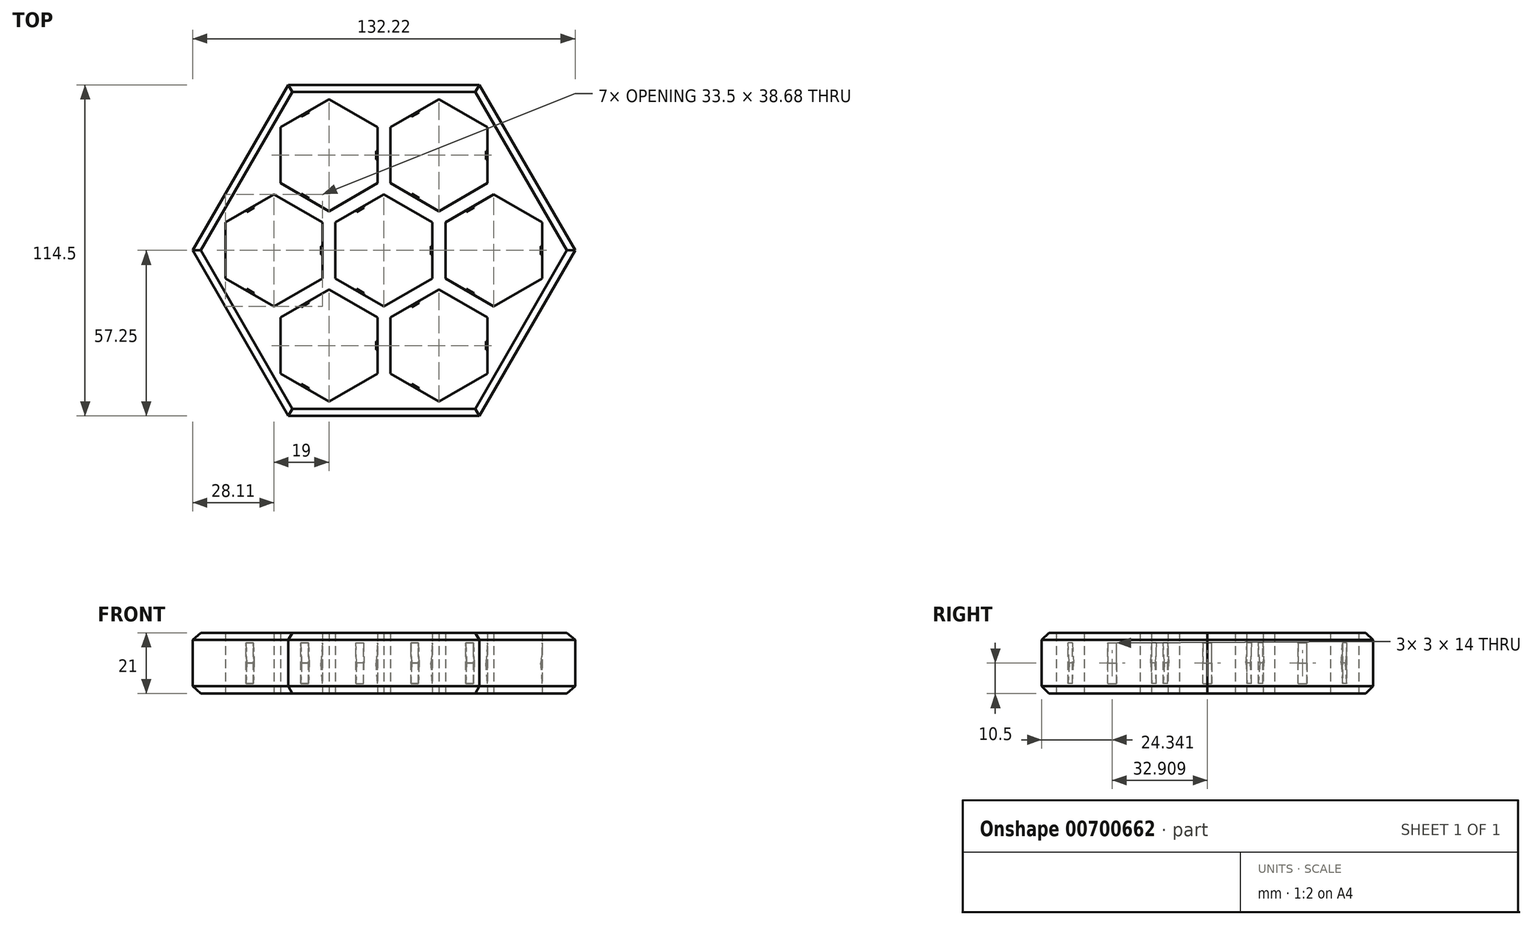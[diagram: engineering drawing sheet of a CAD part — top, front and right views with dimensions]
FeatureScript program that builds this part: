
annotation { "Feature Type Name" : "Feature", "Feature Type Description" : "" }
export const myFeature = defineFeature(function(context is Context, id is Id, definition is map)
    precondition{}
    {
        {
            var Q0;
            Q0=qCreatedBy(makeId("Top.planeOp"),FACE);
            var sketch = newSketch(context, id + "F0", { "sketchPlane" : qUnion([Q0])});
            skCircle(sketch, "E0.cCircle", {"center": v(38, 0) * mm, "radius": 16.75 * mm, "construction": true});
            skLineSegment(sketch, "E0.0", {"start": v(54.75, 9.67) * mm, "end": v(54.75, -9.67) * mm});
            skLineSegment(sketch, "E0.1", {"start": v(54.75, -9.67) * mm, "end": v(38, -19.34) * mm});
            skLineSegment(sketch, "E0.2", {"start": v(38, -19.34) * mm, "end": v(21.25, -9.67) * mm});
            skLineSegment(sketch, "E0.3", {"start": v(21.25, -9.67) * mm, "end": v(21.25, 9.67) * mm});
            skLineSegment(sketch, "E0.4", {"start": v(21.25, 9.67) * mm, "end": v(38, 19.34) * mm});
            skLineSegment(sketch, "E0.5", {"start": v(38, 19.34) * mm, "end": v(54.75, 9.67) * mm});
            skPoint(sketch, "E0.0.midPoint", {"position": v(54.75, 0) * mm});
            skCircle(sketch, "E1.cCircle", {"center": v(19, -32.9) * mm, "radius": 16.75 * mm, "construction": true});
            skLineSegment(sketch, "E1.0", {"start": v(35.75, -23.24) * mm, "end": v(35.75, -42.58) * mm});
            skLineSegment(sketch, "E1.1", {"start": v(35.75, -42.58) * mm, "end": v(19, -52.25) * mm});
            skLineSegment(sketch, "E1.2", {"start": v(19, -52.25) * mm, "end": v(2.25, -42.58) * mm});
            skLineSegment(sketch, "E1.3", {"start": v(2.25, -42.58) * mm, "end": v(2.25, -23.24) * mm});
            skLineSegment(sketch, "E1.4", {"start": v(2.25, -23.24) * mm, "end": v(19, -13.57) * mm});
            skLineSegment(sketch, "E1.5", {"start": v(19, -13.57) * mm, "end": v(35.75, -23.24) * mm});
            skPoint(sketch, "E1.0.midPoint", {"position": v(35.75, -32.9) * mm});
            skCircle(sketch, "E2.cCircle", {"center": v(0, 0) * mm, "radius": 16.75 * mm, "construction": true});
            skLineSegment(sketch, "E2.0", {"start": v(16.75, 9.67) * mm, "end": v(16.75, -9.67) * mm});
            skLineSegment(sketch, "E2.1", {"start": v(16.75, -9.67) * mm, "end": v(0, -19.34) * mm});
            skLineSegment(sketch, "E2.2", {"start": v(0, -19.34) * mm, "end": v(-16.75, -9.67) * mm});
            skLineSegment(sketch, "E2.3", {"start": v(-16.75, -9.67) * mm, "end": v(-16.75, 9.67) * mm});
            skLineSegment(sketch, "E2.4", {"start": v(-16.75, 9.67) * mm, "end": v(0, 19.34) * mm});
            skLineSegment(sketch, "E2.5", {"start": v(0, 19.34) * mm, "end": v(16.75, 9.67) * mm});
            skPoint(sketch, "E2.0.midPoint", {"position": v(16.75, 0) * mm});
            skCircle(sketch, "E3.cCircle", {"center": v(-19, -32.9) * mm, "radius": 16.75 * mm, "construction": true});
            skLineSegment(sketch, "E3.0", {"start": v(-2.25, -23.24) * mm, "end": v(-2.25, -42.58) * mm});
            skLineSegment(sketch, "E3.1", {"start": v(-2.25, -42.58) * mm, "end": v(-19, -52.25) * mm});
            skLineSegment(sketch, "E3.2", {"start": v(-19, -52.25) * mm, "end": v(-35.75, -42.58) * mm});
            skLineSegment(sketch, "E3.3", {"start": v(-35.75, -42.58) * mm, "end": v(-35.75, -23.24) * mm});
            skLineSegment(sketch, "E3.4", {"start": v(-35.75, -23.24) * mm, "end": v(-19, -13.57) * mm});
            skLineSegment(sketch, "E3.5", {"start": v(-19, -13.57) * mm, "end": v(-2.25, -23.24) * mm});
            skPoint(sketch, "E3.0.midPoint", {"position": v(-2.25, -32.9) * mm});
            skCircle(sketch, "E4.cCircle", {"center": v(19, 32.9) * mm, "radius": 16.75 * mm, "construction": true});
            skLineSegment(sketch, "E4.0", {"start": v(35.75, 42.58) * mm, "end": v(35.75, 23.24) * mm});
            skLineSegment(sketch, "E4.1", {"start": v(35.75, 23.24) * mm, "end": v(19, 13.57) * mm});
            skLineSegment(sketch, "E4.2", {"start": v(19, 13.57) * mm, "end": v(2.25, 23.24) * mm});
            skLineSegment(sketch, "E4.3", {"start": v(2.25, 23.24) * mm, "end": v(2.25, 42.58) * mm});
            skLineSegment(sketch, "E4.4", {"start": v(2.25, 42.58) * mm, "end": v(19, 52.25) * mm});
            skLineSegment(sketch, "E4.5", {"start": v(19, 52.25) * mm, "end": v(35.75, 42.58) * mm});
            skPoint(sketch, "E4.0.midPoint", {"position": v(35.75, 32.9) * mm});
            skCircle(sketch, "E5.cCircle", {"center": v(-38, 0) * mm, "radius": 16.75 * mm, "construction": true});
            skLineSegment(sketch, "E5.0", {"start": v(-21.25, 9.67) * mm, "end": v(-21.25, -9.67) * mm});
            skLineSegment(sketch, "E5.1", {"start": v(-21.25, -9.67) * mm, "end": v(-38, -19.34) * mm});
            skLineSegment(sketch, "E5.2", {"start": v(-38, -19.34) * mm, "end": v(-54.75, -9.67) * mm});
            skLineSegment(sketch, "E5.3", {"start": v(-54.75, -9.67) * mm, "end": v(-54.75, 9.67) * mm});
            skLineSegment(sketch, "E5.4", {"start": v(-54.75, 9.67) * mm, "end": v(-38, 19.34) * mm});
            skLineSegment(sketch, "E5.5", {"start": v(-38, 19.34) * mm, "end": v(-21.25, 9.67) * mm});
            skPoint(sketch, "E5.0.midPoint", {"position": v(-21.25, 0) * mm});
            skCircle(sketch, "E6.cCircle", {"center": v(-19, 32.9) * mm, "radius": 16.75 * mm, "construction": true});
            skLineSegment(sketch, "E6.0", {"start": v(-2.25, 42.58) * mm, "end": v(-2.25, 23.24) * mm});
            skLineSegment(sketch, "E6.1", {"start": v(-2.25, 23.24) * mm, "end": v(-19, 13.57) * mm});
            skLineSegment(sketch, "E6.2", {"start": v(-19, 13.57) * mm, "end": v(-35.75, 23.24) * mm});
            skLineSegment(sketch, "E6.3", {"start": v(-35.75, 23.24) * mm, "end": v(-35.75, 42.58) * mm});
            skLineSegment(sketch, "E6.4", {"start": v(-35.75, 42.58) * mm, "end": v(-19, 52.25) * mm});
            skLineSegment(sketch, "E6.5", {"start": v(-19, 52.25) * mm, "end": v(-2.25, 42.58) * mm});
            skPoint(sketch, "E6.0.midPoint", {"position": v(-2.25, 32.9) * mm});
            skCircle(sketch, "E7.cCircle", {"center": v(0, 0) * mm, "radius": 57.25 * mm, "construction": true});
            skLineSegment(sketch, "E7.0", {"start": v(33.05, 57.25) * mm, "end": v(66.1, 0) * mm});
            skLineSegment(sketch, "E7.2", {"start": v(33.05, -57.25) * mm, "end": v(-33.05, -57.25) * mm});
            skLineSegment(sketch, "E7.3", {"start": v(-33.05, -57.25) * mm, "end": v(-66.1, 0) * mm});
            skLineSegment(sketch, "E7.4", {"start": v(-66.1, 0) * mm, "end": v(-33.05, 57.25) * mm});
            skLineSegment(sketch, "E7.5", {"start": v(-33.05, 57.25) * mm, "end": v(33.05, 57.25) * mm});
            skPoint(sketch, "E7.0.midPoint", {"position": v(49.58, 28.62) * mm});
            skLineSegment(sketch, "E8", {"start": v(66.1, 0) * mm, "end": v(33.05, -57.25) * mm});
            skSolve(sketch);
        }
        {
            var Q0;
            Q0=makeQuery(id+"F0.imprint","IMPRINT",FACE,{"disambiguationData":[TD([[makeQuery(id+"F0.imprint","IMPRINT",EDGE,{"derivedFrom":sQuery(id+"F0.wireOp",EDGE,"E0.0")}),1.0]])]});
            extrude(context, id + "F1", {"entities" : qUnion([Q0]), "depth" : 21 * mm, "offsetDistance" : 25 * mm});
        }
        {
            var Q0;
            Q0=makeQuery(id+"F1.opExtrude","CAP_EDGE",EDGE,{"disambiguationData":[OSD([sQuery(id+"F0.wireOp",EDGE,"E7.5")])],"isStart":false});
            var Q1;
            Q1=makeQuery(id+"F1.opExtrude","CAP_EDGE",EDGE,{"disambiguationData":[OSD([sQuery(id+"F0.wireOp",EDGE,"E7.4")])],"isStart":false});
            var Q2;
            Q2=makeQuery(id+"F1.opExtrude","CAP_EDGE",EDGE,{"disambiguationData":[OSD([sQuery(id+"F0.wireOp",EDGE,"E7.3")])],"isStart":false});
            var Q3;
            Q3=makeQuery(id+"F1.opExtrude","CAP_EDGE",EDGE,{"disambiguationData":[OSD([sQuery(id+"F0.wireOp",EDGE,"E7.2")])],"isStart":false});
            var Q4;
            Q4=makeQuery(id+"F1.opExtrude","CAP_EDGE",EDGE,{"disambiguationData":[OSD([sQuery(id+"F0.wireOp",EDGE,"E8")])],"isStart":false});
            var Q5;
            Q5=makeQuery(id+"F1.opExtrude","CAP_EDGE",EDGE,{"disambiguationData":[OSD([sQuery(id+"F0.wireOp",EDGE,"E7.0")])],"isStart":false});
            var Q6;
            Q6=makeQuery(id+"F1.opExtrude","CAP_EDGE",EDGE,{"disambiguationData":[OSD([sQuery(id+"F0.wireOp",EDGE,"E8")])],"isStart":true});
            var Q7;
            Q7=makeQuery(id+"F1.opExtrude","CAP_EDGE",EDGE,{"disambiguationData":[OSD([sQuery(id+"F0.wireOp",EDGE,"E7.2")])],"isStart":true});
            var Q8;
            Q8=makeQuery(id+"F1.opExtrude","CAP_EDGE",EDGE,{"disambiguationData":[OSD([sQuery(id+"F0.wireOp",EDGE,"E7.0")])],"isStart":true});
            var Q9;
            Q9=makeQuery(id+"F1.opExtrude","CAP_EDGE",EDGE,{"disambiguationData":[OSD([sQuery(id+"F0.wireOp",EDGE,"E7.5")])],"isStart":true});
            var Q10;
            Q10=makeQuery(id+"F1.opExtrude","CAP_EDGE",EDGE,{"disambiguationData":[OSD([sQuery(id+"F0.wireOp",EDGE,"E7.4")])],"isStart":true});
            var Q11;
            Q11=makeQuery(id+"F1.opExtrude","CAP_EDGE",EDGE,{"disambiguationData":[OSD([sQuery(id+"F0.wireOp",EDGE,"E7.3")])],"isStart":true});
            chamfer(context, id + "F2", {"entities" : qUnion([Q0, Q1, Q2, Q3, Q4, Q5, Q6, Q7, Q8, Q9, Q10, Q11]), "width" : 2.5 * mm, "tangentPropagation" : true});
        }
        {
            var Q0;
            Q0=makeQuery(id+"F1.opExtrude","SWEPT_FACE",FACE,{"disambiguationData":[OSD([sQuery(id+"F0.wireOp",EDGE,"E6.4")])]});
            var sketch = newSketch(context, id + "F3", { "sketchPlane" : qUnion([Q0])});
            skLineSegment(sketch, "E9.bottom", {"start": v(1.5, 17.5) * mm, "end": v(-1.5, 17.5) * mm});
            skLineSegment(sketch, "E9.top", {"start": v(1.5, 3.5) * mm, "end": v(-1.5, 3.5) * mm});
            skLineSegment(sketch, "E9.left", {"start": v(1.5, 17.5) * mm, "end": v(1.5, 3.5) * mm});
            skLineSegment(sketch, "E9.right", {"start": v(-1.5, 17.5) * mm, "end": v(-1.5, 3.5) * mm});
            skPoint(sketch, "E9.middle", {"position": v(0, 10.5) * mm});
            skSolve(sketch);
        }
        {
            var Q0;
            Q0=makeQuery(id+"F3.imprint","IMPRINT",FACE,{"disambiguationData":[TD([[makeQuery(id+"F3.imprint","IMPRINT",EDGE,{"derivedFrom":sQuery(id+"F3.wireOp",EDGE,"E9.bottom")}),1.0]])]});
            extrude(context, id + "F4", {"entities" : qUnion([Q0]), "operationType" : NewBodyOperationType.ADD, "depth" : .5 * mm, "offsetDistance" : 25 * mm});
        }
        {
            var Q0;
            Q0=makeQuery(id+"F4.opExtrude","CAP_EDGE",EDGE,{"disambiguationData":[OSD([sQuery(id+"F3.wireOp",EDGE,"E9.bottom")])],"isStart":false});
            var Q1;
            Q1=makeQuery(id+"F4.opExtrude","CAP_EDGE",EDGE,{"disambiguationData":[OSD([sQuery(id+"F3.wireOp",EDGE,"E9.top")])],"isStart":false});
            chamfer(context, id + "F5", {"entities" : qUnion([Q0, Q1]), "chamferType" : ChamferType.TWO_OFFSETS, "width1" : 7 * mm, "oppositeDirection" : false, "width2" : .5 * mm, "tangentPropagation" : true});
        }
        {
            var Q0;
            Q0=makeQuery(id+"F1.opExtrude","SWEPT_FACE",FACE,{"disambiguationData":[OSD([sQuery(id+"F0.wireOp",EDGE,"E4.4")])]});
            var sketch = newSketch(context, id + "F6", { "sketchPlane" : qUnion([Q0])});
            skLineSegment(sketch, "E10.bottom", {"start": v(34.4, 3.5) * mm, "end": v(31.4, 3.5) * mm});
            skLineSegment(sketch, "E10.top", {"start": v(34.4, 17.5) * mm, "end": v(31.4, 17.5) * mm});
            skLineSegment(sketch, "E10.left", {"start": v(34.4, 3.5) * mm, "end": v(34.4, 17.5) * mm});
            skLineSegment(sketch, "E10.right", {"start": v(31.4, 3.5) * mm, "end": v(31.4, 17.5) * mm});
            skPoint(sketch, "E10.middle", {"position": v(32.9, 10.5) * mm});
            skLineSegment(sketch, "E11.bottom", {"start": v(-31.4, 3.5) * mm, "end": v(-34.4, 3.5) * mm});
            skLineSegment(sketch, "E11.top", {"start": v(-31.4, 17.5) * mm, "end": v(-34.4, 17.5) * mm});
            skLineSegment(sketch, "E11.left", {"start": v(-31.4, 3.5) * mm, "end": v(-31.4, 17.5) * mm});
            skLineSegment(sketch, "E11.right", {"start": v(-34.4, 3.5) * mm, "end": v(-34.4, 17.5) * mm});
            skPoint(sketch, "E11.middle", {"position": v(-32.9, 10.5) * mm});
            skSolve(sketch);
        }
        {
            var Q0;
            Q0=makeQuery(id+"F6.imprint","IMPRINT",FACE,{"disambiguationData":[TD([[makeQuery(id+"F6.imprint","IMPRINT",EDGE,{"derivedFrom":sQuery(id+"F6.wireOp",EDGE,"E10.bottom")}),-1.0]])]});
            var Q1;
            Q1=makeQuery(id+"F6.imprint","IMPRINT",FACE,{"disambiguationData":[TD([[makeQuery(id+"F6.imprint","IMPRINT",EDGE,{"derivedFrom":sQuery(id+"F6.wireOp",EDGE,"E11.bottom")}),-1.0]])]});
            extrude(context, id + "F7", {"entities" : qUnion([Q0, Q1]), "operationType" : NewBodyOperationType.ADD, "depth" : .5 * mm, "offsetDistance" : 25 * mm});
        }
        {
            var Q0;
            Q0=makeQuery(id+"F7.opExtrude","CAP_EDGE",EDGE,{"disambiguationData":[OSD([sQuery(id+"F6.wireOp",EDGE,"E11.top")])],"isStart":false});
            var Q1;
            Q1=makeQuery(id+"F7.opExtrude","CAP_EDGE",EDGE,{"disambiguationData":[OSD([sQuery(id+"F6.wireOp",EDGE,"E11.bottom")])],"isStart":false});
            var Q2;
            Q2=makeQuery(id+"F7.opExtrude","CAP_EDGE",EDGE,{"disambiguationData":[OSD([sQuery(id+"F6.wireOp",EDGE,"E10.top")])],"isStart":false});
            chamfer(context, id + "F8", {"entities" : qUnion([Q0, Q1, Q2]), "chamferType" : ChamferType.TWO_OFFSETS, "width1" : 7 * mm, "oppositeDirection" : false, "width2" : .5 * mm, "tangentPropagation" : true});
        }
        {
            var Q0;
            Q0=makeQuery(id+"F7.opExtrude","CAP_EDGE",EDGE,{"disambiguationData":[OSD([sQuery(id+"F6.wireOp",EDGE,"E10.bottom")])],"isStart":false});
            chamfer(context, id + "F9", {"entities" : qUnion([Q0]), "chamferType" : ChamferType.TWO_OFFSETS, "width1" : 7 * mm, "oppositeDirection" : true, "width2" : .5 * mm, "tangentPropagation" : true});
        }
        {
            var Q0;
            Q0=makeQuery(id+"F1.opExtrude","SWEPT_FACE",FACE,{"disambiguationData":[OSD([sQuery(id+"F0.wireOp",EDGE,"E2.4")])]});
            var sketch = newSketch(context, id + "F10", { "sketchPlane" : qUnion([Q0])});
            skLineSegment(sketch, "E12.bottom", {"start": v(1.5, 3.5) * mm, "end": v(-1.5, 3.5) * mm});
            skLineSegment(sketch, "E12.top", {"start": v(1.5, 17.5) * mm, "end": v(-1.5, 17.5) * mm});
            skLineSegment(sketch, "E12.left", {"start": v(1.5, 3.5) * mm, "end": v(1.5, 17.5) * mm});
            skLineSegment(sketch, "E12.right", {"start": v(-1.5, 3.5) * mm, "end": v(-1.5, 17.5) * mm});
            skPoint(sketch, "E12.middle", {"position": v(0, 10.5) * mm});
            skSolve(sketch);
        }
        {
            var Q0;
            Q0=makeQuery(id+"F10.imprint","IMPRINT",FACE,{"disambiguationData":[TD([[makeQuery(id+"F10.imprint","IMPRINT",EDGE,{"derivedFrom":sQuery(id+"F10.wireOp",EDGE,"E12.bottom")}),-1.0]])]});
            extrude(context, id + "F11", {"entities" : qUnion([Q0]), "operationType" : NewBodyOperationType.ADD, "depth" : .5 * mm, "offsetDistance" : 25 * mm});
        }
        {
            var Q0;
            Q0=makeQuery(id+"F11.opExtrude","CAP_EDGE",EDGE,{"disambiguationData":[OSD([sQuery(id+"F10.wireOp",EDGE,"E12.top")])],"isStart":false});
            var Q1;
            Q1=makeQuery(id+"F11.opExtrude","CAP_EDGE",EDGE,{"disambiguationData":[OSD([sQuery(id+"F10.wireOp",EDGE,"E12.bottom")])],"isStart":false});
            chamfer(context, id + "F12", {"entities" : qUnion([Q0, Q1]), "chamferType" : ChamferType.TWO_OFFSETS, "width1" : 7 * mm, "oppositeDirection" : false, "width2" : .5 * mm, "tangentPropagation" : true});
        }
        {
            var Q0;
            Q0=makeQuery(id+"F1.opExtrude","SWEPT_FACE",FACE,{"disambiguationData":[OSD([sQuery(id+"F0.wireOp",EDGE,"E0.4")])]});
            var sketch = newSketch(context, id + "F13", { "sketchPlane" : qUnion([Q0])});
            skLineSegment(sketch, "E13.bottom", {"start": v(34.4, 3.5) * mm, "end": v(31.4, 3.5) * mm});
            skLineSegment(sketch, "E13.top", {"start": v(34.4, 17.5) * mm, "end": v(31.4, 17.5) * mm});
            skLineSegment(sketch, "E13.left", {"start": v(34.4, 3.5) * mm, "end": v(34.4, 17.5) * mm});
            skLineSegment(sketch, "E13.right", {"start": v(31.4, 3.5) * mm, "end": v(31.4, 17.5) * mm});
            skPoint(sketch, "E13.middle", {"position": v(32.9, 10.5) * mm});
            skLineSegment(sketch, "E14.bottom", {"start": v(-31.4, 3.5) * mm, "end": v(-34.4, 3.5) * mm});
            skLineSegment(sketch, "E14.top", {"start": v(-31.4, 17.5) * mm, "end": v(-34.4, 17.5) * mm});
            skLineSegment(sketch, "E14.left", {"start": v(-31.4, 3.5) * mm, "end": v(-31.4, 17.5) * mm});
            skLineSegment(sketch, "E14.right", {"start": v(-34.4, 3.5) * mm, "end": v(-34.4, 17.5) * mm});
            skPoint(sketch, "E14.middle", {"position": v(-32.9, 10.5) * mm});
            skSolve(sketch);
        }
        {
            var Q0;
            Q0=makeQuery(id+"F13.imprint","IMPRINT",FACE,{"disambiguationData":[TD([[makeQuery(id+"F13.imprint","IMPRINT",EDGE,{"derivedFrom":sQuery(id+"F13.wireOp",EDGE,"E14.bottom")}),-1.0]])]});
            var Q1;
            Q1=makeQuery(id+"F13.imprint","IMPRINT",FACE,{"disambiguationData":[TD([[makeQuery(id+"F13.imprint","IMPRINT",EDGE,{"derivedFrom":sQuery(id+"F13.wireOp",EDGE,"E13.bottom")}),-1.0]])]});
            extrude(context, id + "F14", {"entities" : qUnion([Q0, Q1]), "operationType" : NewBodyOperationType.ADD, "depth" : .5 * mm, "offsetDistance" : 25 * mm});
        }
        {
            var Q0;
            Q0=makeQuery(id+"F14.opExtrude","CAP_EDGE",EDGE,{"disambiguationData":[OSD([sQuery(id+"F13.wireOp",EDGE,"E14.top")])],"isStart":false});
            var Q1;
            Q1=makeQuery(id+"F14.opExtrude","CAP_EDGE",EDGE,{"disambiguationData":[OSD([sQuery(id+"F13.wireOp",EDGE,"E14.bottom")])],"isStart":false});
            var Q2;
            Q2=makeQuery(id+"F14.opExtrude","CAP_EDGE",EDGE,{"disambiguationData":[OSD([sQuery(id+"F13.wireOp",EDGE,"E13.top")])],"isStart":false});
            chamfer(context, id + "F15", {"entities" : qUnion([Q0, Q1, Q2]), "chamferType" : ChamferType.TWO_OFFSETS, "width1" : 7 * mm, "oppositeDirection" : false, "width2" : .5 * mm, "tangentPropagation" : true});
        }
        {
            var Q0;
            Q0=makeQuery(id+"F14.opExtrude","CAP_EDGE",EDGE,{"disambiguationData":[OSD([sQuery(id+"F13.wireOp",EDGE,"E13.bottom")])],"isStart":false});
            chamfer(context, id + "F16", {"entities" : qUnion([Q0]), "chamferType" : ChamferType.TWO_OFFSETS, "width1" : 7 * mm, "oppositeDirection" : true, "width2" : .5 * mm, "tangentPropagation" : true});
        }
        {
            var Q0;
            Q0=makeQuery(id+"F1.opExtrude","SWEPT_FACE",FACE,{"disambiguationData":[OSD([sQuery(id+"F0.wireOp",EDGE,"E1.4")])]});
            var sketch = newSketch(context, id + "F17", { "sketchPlane" : qUnion([Q0])});
            skLineSegment(sketch, "E15.bottom", {"start": v(1.5, 3.5) * mm, "end": v(-1.5, 3.5) * mm});
            skLineSegment(sketch, "E15.top", {"start": v(1.5, 17.5) * mm, "end": v(-1.5, 17.5) * mm});
            skLineSegment(sketch, "E15.left", {"start": v(1.5, 3.5) * mm, "end": v(1.5, 17.5) * mm});
            skLineSegment(sketch, "E15.right", {"start": v(-1.5, 3.5) * mm, "end": v(-1.5, 17.5) * mm});
            skPoint(sketch, "E15.middle", {"position": v(0, 10.5) * mm});
            skSolve(sketch);
        }
        {
            var Q0;
            Q0=makeQuery(id+"F17.imprint","IMPRINT",FACE,{"disambiguationData":[TD([[makeQuery(id+"F17.imprint","IMPRINT",EDGE,{"derivedFrom":sQuery(id+"F17.wireOp",EDGE,"E15.bottom")}),-1.0]])]});
            extrude(context, id + "F18", {"entities" : qUnion([Q0]), "operationType" : NewBodyOperationType.ADD, "depth" : .5 * mm, "offsetDistance" : 25 * mm});
        }
        {
            var Q0;
            Q0=makeQuery(id+"F18.opExtrude","CAP_EDGE",EDGE,{"disambiguationData":[OSD([sQuery(id+"F17.wireOp",EDGE,"E15.top")])],"isStart":false});
            var Q1;
            Q1=makeQuery(id+"F18.opExtrude","CAP_EDGE",EDGE,{"disambiguationData":[OSD([sQuery(id+"F17.wireOp",EDGE,"E15.bottom")])],"isStart":false});
            chamfer(context, id + "F19", {"entities" : qUnion([Q0, Q1]), "chamferType" : ChamferType.TWO_OFFSETS, "width1" : 7 * mm, "oppositeDirection" : false, "width2" : .5 * mm, "tangentPropagation" : true});
        }
        {
            var Q0;
            Q0=makeQuery(id+"F1.opExtrude","SWEPT_FACE",FACE,{"disambiguationData":[OSD([sQuery(id+"F0.wireOp",EDGE,"E0.0")])]});
            var sketch = newSketch(context, id + "F20", { "sketchPlane" : qUnion([Q0])});
            skLineSegment(sketch, "E16.bottom", {"start": v(1.5, 3.5) * mm, "end": v(-1.5, 3.5) * mm});
            skLineSegment(sketch, "E16.top", {"start": v(1.5, 17.5) * mm, "end": v(-1.5, 17.5) * mm});
            skLineSegment(sketch, "E16.left", {"start": v(1.5, 3.5) * mm, "end": v(1.5, 17.5) * mm});
            skLineSegment(sketch, "E16.right", {"start": v(-1.5, 3.5) * mm, "end": v(-1.5, 17.5) * mm});
            skPoint(sketch, "E16.middle", {"position": v(0, 10.5) * mm});
            skSolve(sketch);
        }
        {
            var Q0;
            Q0=makeQuery(id+"F20.imprint","IMPRINT",FACE,{"disambiguationData":[TD([[makeQuery(id+"F20.imprint","IMPRINT",EDGE,{"derivedFrom":sQuery(id+"F20.wireOp",EDGE,"E16.bottom")}),-1.0]])]});
            extrude(context, id + "F21", {"entities" : qUnion([Q0]), "operationType" : NewBodyOperationType.ADD, "depth" : .5 * mm, "offsetDistance" : 25 * mm});
        }
        {
            var Q0;
            Q0=makeQuery(id+"F21.opExtrude","CAP_EDGE",EDGE,{"disambiguationData":[OSD([sQuery(id+"F20.wireOp",EDGE,"E16.top")])],"isStart":false});
            var Q1;
            Q1=makeQuery(id+"F21.opExtrude","CAP_EDGE",EDGE,{"disambiguationData":[OSD([sQuery(id+"F20.wireOp",EDGE,"E16.bottom")])],"isStart":false});
            chamfer(context, id + "F22", {"entities" : qUnion([Q0, Q1]), "chamferType" : ChamferType.TWO_OFFSETS, "width1" : 7 * mm, "oppositeDirection" : false, "width2" : .5 * mm, "tangentPropagation" : true});
        }
        {
            var Q0;
            Q0=makeQuery(id+"F1.opExtrude","SWEPT_FACE",FACE,{"disambiguationData":[OSD([sQuery(id+"F0.wireOp",EDGE,"E1.0")])]});
            var sketch = newSketch(context, id + "F23", { "sketchPlane" : qUnion([Q0])});
            skLineSegment(sketch, "E17.bottom", {"start": v(34.4, 3.5) * mm, "end": v(31.4, 3.5) * mm});
            skLineSegment(sketch, "E17.top", {"start": v(34.4, 17.5) * mm, "end": v(31.4, 17.5) * mm});
            skLineSegment(sketch, "E17.left", {"start": v(34.4, 3.5) * mm, "end": v(34.4, 17.5) * mm});
            skLineSegment(sketch, "E17.right", {"start": v(31.4, 3.5) * mm, "end": v(31.4, 17.5) * mm});
            skPoint(sketch, "E17.middle", {"position": v(32.9, 10.5) * mm});
            skLineSegment(sketch, "E18.bottom", {"start": v(-31.4, 3.5) * mm, "end": v(-34.4, 3.5) * mm});
            skLineSegment(sketch, "E18.top", {"start": v(-31.4, 17.5) * mm, "end": v(-34.4, 17.5) * mm});
            skLineSegment(sketch, "E18.left", {"start": v(-31.4, 3.5) * mm, "end": v(-31.4, 17.5) * mm});
            skLineSegment(sketch, "E18.right", {"start": v(-34.4, 3.5) * mm, "end": v(-34.4, 17.5) * mm});
            skPoint(sketch, "E18.middle", {"position": v(-32.9, 10.5) * mm});
            skSolve(sketch);
        }
        {
            var Q0;
            Q0=makeQuery(id+"F23.imprint","IMPRINT",FACE,{"disambiguationData":[TD([[makeQuery(id+"F23.imprint","IMPRINT",EDGE,{"derivedFrom":sQuery(id+"F23.wireOp",EDGE,"E18.bottom")}),-1.0]])]});
            var Q1;
            Q1=makeQuery(id+"F23.imprint","IMPRINT",FACE,{"disambiguationData":[TD([[makeQuery(id+"F23.imprint","IMPRINT",EDGE,{"derivedFrom":sQuery(id+"F23.wireOp",EDGE,"E17.bottom")}),-1.0]])]});
            extrude(context, id + "F24", {"entities" : qUnion([Q0, Q1]), "operationType" : NewBodyOperationType.ADD, "depth" : .5 * mm, "offsetDistance" : 25 * mm});
        }
        {
            var Q0;
            Q0=makeQuery(id+"F24.opExtrude","CAP_EDGE",EDGE,{"disambiguationData":[OSD([sQuery(id+"F23.wireOp",EDGE,"E17.top")])],"isStart":false});
            var Q1;
            Q1=makeQuery(id+"F24.opExtrude","CAP_EDGE",EDGE,{"disambiguationData":[OSD([sQuery(id+"F23.wireOp",EDGE,"E17.bottom")])],"isStart":false});
            var Q2;
            Q2=makeQuery(id+"F24.opExtrude","CAP_EDGE",EDGE,{"disambiguationData":[OSD([sQuery(id+"F23.wireOp",EDGE,"E18.top")])],"isStart":false});
            chamfer(context, id + "F25", {"entities" : qUnion([Q0, Q1, Q2]), "chamferType" : ChamferType.TWO_OFFSETS, "width1" : 7 * mm, "oppositeDirection" : false, "width2" : .5 * mm, "tangentPropagation" : true});
        }
        {
            var Q0;
            Q0=makeQuery(id+"F24.opExtrude","CAP_EDGE",EDGE,{"disambiguationData":[OSD([sQuery(id+"F23.wireOp",EDGE,"E18.bottom")])],"isStart":false});
            chamfer(context, id + "F26", {"entities" : qUnion([Q0]), "chamferType" : ChamferType.TWO_OFFSETS, "width1" : 7 * mm, "oppositeDirection" : true, "width2" : .5 * mm, "tangentPropagation" : true});
        }
        {
            var Q0;
            Q0=makeQuery(id+"F1.opExtrude","SWEPT_FACE",FACE,{"disambiguationData":[OSD([sQuery(id+"F0.wireOp",EDGE,"E2.0")])]});
            var sketch = newSketch(context, id + "F27", { "sketchPlane" : qUnion([Q0])});
            skLineSegment(sketch, "E19.bottom", {"start": v(1.5, 3.5) * mm, "end": v(-1.5, 3.5) * mm});
            skLineSegment(sketch, "E19.top", {"start": v(1.5, 17.5) * mm, "end": v(-1.5, 17.5) * mm});
            skLineSegment(sketch, "E19.left", {"start": v(1.5, 3.5) * mm, "end": v(1.5, 17.5) * mm});
            skLineSegment(sketch, "E19.right", {"start": v(-1.5, 3.5) * mm, "end": v(-1.5, 17.5) * mm});
            skPoint(sketch, "E19.middle", {"position": v(0, 10.5) * mm});
            skSolve(sketch);
        }
        {
            var Q0;
            Q0=makeQuery(id+"F27.imprint","IMPRINT",FACE,{"disambiguationData":[TD([[makeQuery(id+"F27.imprint","IMPRINT",EDGE,{"derivedFrom":sQuery(id+"F27.wireOp",EDGE,"E19.bottom")}),-1.0]])]});
            extrude(context, id + "F28", {"entities" : qUnion([Q0]), "operationType" : NewBodyOperationType.ADD, "depth" : .5 * mm, "offsetDistance" : 25 * mm});
        }
        {
            var Q0;
            Q0=makeQuery(id+"F28.opExtrude","CAP_EDGE",EDGE,{"disambiguationData":[OSD([sQuery(id+"F27.wireOp",EDGE,"E19.top")])],"isStart":false});
            var Q1;
            Q1=makeQuery(id+"F28.opExtrude","CAP_EDGE",EDGE,{"disambiguationData":[OSD([sQuery(id+"F27.wireOp",EDGE,"E19.bottom")])],"isStart":false});
            chamfer(context, id + "F29", {"entities" : qUnion([Q0, Q1]), "chamferType" : ChamferType.TWO_OFFSETS, "width1" : 7 * mm, "oppositeDirection" : false, "width2" : .5 * mm, "tangentPropagation" : true});
        }
        {
            var Q0;
            Q0=makeQuery(id+"F1.opExtrude","SWEPT_FACE",FACE,{"disambiguationData":[OSD([sQuery(id+"F0.wireOp",EDGE,"E3.0")])]});
            var sketch = newSketch(context, id + "F30", { "sketchPlane" : qUnion([Q0])});
            skLineSegment(sketch, "E20.bottom", {"start": v(34.4, 3.5) * mm, "end": v(31.4, 3.5) * mm});
            skLineSegment(sketch, "E20.top", {"start": v(34.4, 17.5) * mm, "end": v(31.4, 17.5) * mm});
            skLineSegment(sketch, "E20.left", {"start": v(34.4, 3.5) * mm, "end": v(34.4, 17.5) * mm});
            skLineSegment(sketch, "E20.right", {"start": v(31.4, 3.5) * mm, "end": v(31.4, 17.5) * mm});
            skPoint(sketch, "E20.middle", {"position": v(32.9, 10.5) * mm});
            skLineSegment(sketch, "E21.bottom", {"start": v(-31.4, 3.5) * mm, "end": v(-34.4, 3.5) * mm});
            skLineSegment(sketch, "E21.top", {"start": v(-31.4, 17.5) * mm, "end": v(-34.4, 17.5) * mm});
            skLineSegment(sketch, "E21.left", {"start": v(-31.4, 3.5) * mm, "end": v(-31.4, 17.5) * mm});
            skLineSegment(sketch, "E21.right", {"start": v(-34.4, 3.5) * mm, "end": v(-34.4, 17.5) * mm});
            skPoint(sketch, "E21.middle", {"position": v(-32.9, 10.5) * mm});
            skSolve(sketch);
        }
        {
            var Q0;
            Q0=makeQuery(id+"F30.imprint","IMPRINT",FACE,{"disambiguationData":[TD([[makeQuery(id+"F30.imprint","IMPRINT",EDGE,{"derivedFrom":sQuery(id+"F30.wireOp",EDGE,"E21.bottom")}),-1.0]])]});
            var Q1;
            Q1=makeQuery(id+"F30.imprint","IMPRINT",FACE,{"disambiguationData":[TD([[makeQuery(id+"F30.imprint","IMPRINT",EDGE,{"derivedFrom":sQuery(id+"F30.wireOp",EDGE,"E20.bottom")}),-1.0]])]});
            extrude(context, id + "F31", {"entities" : qUnion([Q0, Q1]), "operationType" : NewBodyOperationType.ADD, "depth" : .5 * mm, "offsetDistance" : 25 * mm});
        }
        {
            var Q0;
            Q0=makeQuery(id+"F31.opExtrude","CAP_EDGE",EDGE,{"disambiguationData":[OSD([sQuery(id+"F30.wireOp",EDGE,"E21.top")])],"isStart":false});
            var Q1;
            Q1=makeQuery(id+"F31.opExtrude","CAP_EDGE",EDGE,{"disambiguationData":[OSD([sQuery(id+"F30.wireOp",EDGE,"E21.bottom")])],"isStart":false});
            var Q2;
            Q2=makeQuery(id+"F31.opExtrude","CAP_EDGE",EDGE,{"disambiguationData":[OSD([sQuery(id+"F30.wireOp",EDGE,"E20.top")])],"isStart":false});
            chamfer(context, id + "F32", {"entities" : qUnion([Q0, Q1, Q2]), "chamferType" : ChamferType.TWO_OFFSETS, "width1" : 7 * mm, "oppositeDirection" : false, "width2" : .5 * mm, "tangentPropagation" : true});
        }
        {
            var Q0;
            Q0=makeQuery(id+"F31.opExtrude","CAP_EDGE",EDGE,{"disambiguationData":[OSD([sQuery(id+"F30.wireOp",EDGE,"E20.bottom")])],"isStart":false});
            chamfer(context, id + "F33", {"entities" : qUnion([Q0]), "chamferType" : ChamferType.TWO_OFFSETS, "width1" : 7 * mm, "oppositeDirection" : true, "width2" : .5 * mm, "tangentPropagation" : true});
        }
        {
            var Q0;
            Q0=makeQuery(id+"F1.opExtrude","SWEPT_FACE",FACE,{"disambiguationData":[OSD([sQuery(id+"F0.wireOp",EDGE,"E5.0")])]});
            var sketch = newSketch(context, id + "F34", { "sketchPlane" : qUnion([Q0])});
            skLineSegment(sketch, "E22.bottom", {"start": v(1.5, 3.5) * mm, "end": v(-1.5, 3.5) * mm});
            skLineSegment(sketch, "E22.top", {"start": v(1.5, 17.5) * mm, "end": v(-1.5, 17.5) * mm});
            skLineSegment(sketch, "E22.left", {"start": v(1.5, 3.5) * mm, "end": v(1.5, 17.5) * mm});
            skLineSegment(sketch, "E22.right", {"start": v(-1.5, 3.5) * mm, "end": v(-1.5, 17.5) * mm});
            skPoint(sketch, "E22.middle", {"position": v(0, 10.5) * mm});
            skSolve(sketch);
        }
        {
            var Q0;
            Q0=makeQuery(id+"F34.imprint","IMPRINT",FACE,{"disambiguationData":[TD([[makeQuery(id+"F34.imprint","IMPRINT",EDGE,{"derivedFrom":sQuery(id+"F34.wireOp",EDGE,"E22.bottom")}),-1.0]])]});
            extrude(context, id + "F35", {"entities" : qUnion([Q0]), "operationType" : NewBodyOperationType.ADD, "depth" : .5 * mm, "offsetDistance" : 25 * mm});
        }
        {
            var Q0;
            Q0=makeQuery(id+"F35.opExtrude","CAP_EDGE",EDGE,{"disambiguationData":[OSD([sQuery(id+"F34.wireOp",EDGE,"E22.top")])],"isStart":false});
            var Q1;
            Q1=makeQuery(id+"F35.opExtrude","CAP_EDGE",EDGE,{"disambiguationData":[OSD([sQuery(id+"F34.wireOp",EDGE,"E22.bottom")])],"isStart":false});
            chamfer(context, id + "F36", {"entities" : qUnion([Q0, Q1]), "chamferType" : ChamferType.TWO_OFFSETS, "width1" : 7 * mm, "oppositeDirection" : false, "width2" : .5 * mm, "tangentPropagation" : true});
        }
        {
            var Q0;
            Q0=makeQuery(id+"F1.opExtrude","SWEPT_FACE",FACE,{"disambiguationData":[OSD([sQuery(id+"F0.wireOp",EDGE,"E3.2")])]});
            var sketch = newSketch(context, id + "F37", { "sketchPlane" : qUnion([Q0])});
            skLineSegment(sketch, "E23.bottom", {"start": v(1.5, 3.5) * mm, "end": v(-1.5, 3.5) * mm});
            skLineSegment(sketch, "E23.top", {"start": v(1.5, 17.5) * mm, "end": v(-1.5, 17.5) * mm});
            skLineSegment(sketch, "E23.left", {"start": v(1.5, 3.5) * mm, "end": v(1.5, 17.5) * mm});
            skLineSegment(sketch, "E23.right", {"start": v(-1.5, 3.5) * mm, "end": v(-1.5, 17.5) * mm});
            skPoint(sketch, "E23.middle", {"position": v(0, 10.5) * mm});
            skSolve(sketch);
        }
        {
            var Q0;
            Q0=makeQuery(id+"F37.imprint","IMPRINT",FACE,{"disambiguationData":[TD([[makeQuery(id+"F37.imprint","IMPRINT",EDGE,{"derivedFrom":sQuery(id+"F37.wireOp",EDGE,"E23.bottom")}),-1.0]])]});
            extrude(context, id + "F38", {"entities" : qUnion([Q0]), "operationType" : NewBodyOperationType.ADD, "depth" : .5 * mm, "offsetDistance" : 25 * mm});
        }
        {
            var Q0;
            Q0=makeQuery(id+"F38.opExtrude","CAP_EDGE",EDGE,{"disambiguationData":[OSD([sQuery(id+"F37.wireOp",EDGE,"E23.top")])],"isStart":false});
            var Q1;
            Q1=makeQuery(id+"F38.opExtrude","CAP_EDGE",EDGE,{"disambiguationData":[OSD([sQuery(id+"F37.wireOp",EDGE,"E23.bottom")])],"isStart":false});
            chamfer(context, id + "F39", {"entities" : qUnion([Q0, Q1]), "chamferType" : ChamferType.TWO_OFFSETS, "width1" : 7 * mm, "oppositeDirection" : false, "width2" : .5 * mm, "tangentPropagation" : true});
        }
        {
            var Q0;
            Q0=makeQuery(id+"F1.opExtrude","SWEPT_FACE",FACE,{"disambiguationData":[OSD([sQuery(id+"F0.wireOp",EDGE,"E5.2")])]});
            var sketch = newSketch(context, id + "F40", { "sketchPlane" : qUnion([Q0])});
            skLineSegment(sketch, "E24.bottom", {"start": v(34.4, 3.5) * mm, "end": v(31.4, 3.5) * mm});
            skLineSegment(sketch, "E24.top", {"start": v(34.4, 17.5) * mm, "end": v(31.4, 17.5) * mm});
            skLineSegment(sketch, "E24.left", {"start": v(34.4, 3.5) * mm, "end": v(34.4, 17.5) * mm});
            skLineSegment(sketch, "E24.right", {"start": v(31.4, 3.5) * mm, "end": v(31.4, 17.5) * mm});
            skPoint(sketch, "E24.middle", {"position": v(32.9, 10.5) * mm});
            skLineSegment(sketch, "E25.bottom", {"start": v(-31.4, 3.5) * mm, "end": v(-34.4, 3.5) * mm});
            skLineSegment(sketch, "E25.top", {"start": v(-31.4, 17.5) * mm, "end": v(-34.4, 17.5) * mm});
            skLineSegment(sketch, "E25.left", {"start": v(-31.4, 3.5) * mm, "end": v(-31.4, 17.5) * mm});
            skLineSegment(sketch, "E25.right", {"start": v(-34.4, 3.5) * mm, "end": v(-34.4, 17.5) * mm});
            skPoint(sketch, "E25.middle", {"position": v(-32.9, 10.5) * mm});
            skSolve(sketch);
        }
        {
            var Q0;
            Q0=makeQuery(id+"F40.imprint","IMPRINT",FACE,{"disambiguationData":[TD([[makeQuery(id+"F40.imprint","IMPRINT",EDGE,{"derivedFrom":sQuery(id+"F40.wireOp",EDGE,"E25.bottom")}),-1.0]])]});
            var Q1;
            Q1=makeQuery(id+"F40.imprint","IMPRINT",FACE,{"disambiguationData":[TD([[makeQuery(id+"F40.imprint","IMPRINT",EDGE,{"derivedFrom":sQuery(id+"F40.wireOp",EDGE,"E24.bottom")}),-1.0]])]});
            extrude(context, id + "F41", {"entities" : qUnion([Q0, Q1]), "operationType" : NewBodyOperationType.ADD, "depth" : .5 * mm, "offsetDistance" : 25 * mm});
        }
        {
            var Q0;
            Q0=makeQuery(id+"F41.opExtrude","CAP_EDGE",EDGE,{"disambiguationData":[OSD([sQuery(id+"F40.wireOp",EDGE,"E25.top")])],"isStart":false});
            var Q1;
            Q1=makeQuery(id+"F41.opExtrude","CAP_EDGE",EDGE,{"disambiguationData":[OSD([sQuery(id+"F40.wireOp",EDGE,"E25.bottom")])],"isStart":false});
            var Q2;
            Q2=makeQuery(id+"F41.opExtrude","CAP_EDGE",EDGE,{"disambiguationData":[OSD([sQuery(id+"F40.wireOp",EDGE,"E24.top")])],"isStart":false});
            chamfer(context, id + "F42", {"entities" : qUnion([Q0, Q1, Q2]), "chamferType" : ChamferType.TWO_OFFSETS, "width1" : 7 * mm, "oppositeDirection" : false, "width2" : .5 * mm, "tangentPropagation" : true});
        }
        {
            var Q0;
            Q0=makeQuery(id+"F41.opExtrude","CAP_EDGE",EDGE,{"disambiguationData":[OSD([sQuery(id+"F40.wireOp",EDGE,"E24.bottom")])],"isStart":false});
            chamfer(context, id + "F43", {"entities" : qUnion([Q0]), "chamferType" : ChamferType.TWO_OFFSETS, "width1" : 7 * mm, "oppositeDirection" : true, "width2" : .5 * mm, "tangentPropagation" : true});
        }
        {
            var Q0;
            Q0=makeQuery(id+"F1.opExtrude","SWEPT_FACE",FACE,{"disambiguationData":[OSD([sQuery(id+"F0.wireOp",EDGE,"E2.2")])]});
            var sketch = newSketch(context, id + "F44", { "sketchPlane" : qUnion([Q0])});
            skLineSegment(sketch, "E26.bottom", {"start": v(1.5, 3.5) * mm, "end": v(-1.5, 3.5) * mm});
            skLineSegment(sketch, "E26.top", {"start": v(1.5, 17.5) * mm, "end": v(-1.5, 17.5) * mm});
            skLineSegment(sketch, "E26.left", {"start": v(1.5, 3.5) * mm, "end": v(1.5, 17.5) * mm});
            skLineSegment(sketch, "E26.right", {"start": v(-1.5, 3.5) * mm, "end": v(-1.5, 17.5) * mm});
            skPoint(sketch, "E26.middle", {"position": v(0, 10.5) * mm});
            skSolve(sketch);
        }
        {
            var Q0;
            Q0=makeQuery(id+"F44.imprint","IMPRINT",FACE,{"disambiguationData":[TD([[makeQuery(id+"F44.imprint","IMPRINT",EDGE,{"derivedFrom":sQuery(id+"F44.wireOp",EDGE,"E26.bottom")}),-1.0]])]});
            extrude(context, id + "F45", {"entities" : qUnion([Q0]), "operationType" : NewBodyOperationType.ADD, "depth" : .5 * mm, "offsetDistance" : 25 * mm});
        }
        {
            var Q0;
            Q0=makeQuery(id+"F45.opExtrude","CAP_EDGE",EDGE,{"disambiguationData":[OSD([sQuery(id+"F44.wireOp",EDGE,"E26.top")])],"isStart":false});
            var Q1;
            Q1=makeQuery(id+"F45.opExtrude","CAP_EDGE",EDGE,{"disambiguationData":[OSD([sQuery(id+"F44.wireOp",EDGE,"E26.bottom")])],"isStart":false});
            chamfer(context, id + "F46", {"entities" : qUnion([Q0, Q1]), "chamferType" : ChamferType.TWO_OFFSETS, "width1" : 7 * mm, "oppositeDirection" : false, "width2" : .5 * mm, "tangentPropagation" : true});
        }
        {
            var Q0;
            Q0=makeQuery(id+"F1.opExtrude","SWEPT_FACE",FACE,{"disambiguationData":[OSD([sQuery(id+"F0.wireOp",EDGE,"E6.2")])]});
            var sketch = newSketch(context, id + "F47", { "sketchPlane" : qUnion([Q0])});
            skLineSegment(sketch, "E27.bottom", {"start": v(34.4, 3.5) * mm, "end": v(31.4, 3.5) * mm});
            skLineSegment(sketch, "E27.top", {"start": v(34.4, 17.5) * mm, "end": v(31.4, 17.5) * mm});
            skLineSegment(sketch, "E27.left", {"start": v(34.4, 3.5) * mm, "end": v(34.4, 17.5) * mm});
            skLineSegment(sketch, "E27.right", {"start": v(31.4, 3.5) * mm, "end": v(31.4, 17.5) * mm});
            skPoint(sketch, "E27.middle", {"position": v(32.9, 10.5) * mm});
            skLineSegment(sketch, "E28.bottom", {"start": v(-31.4, 3.5) * mm, "end": v(-34.4, 3.5) * mm});
            skLineSegment(sketch, "E28.top", {"start": v(-31.4, 17.5) * mm, "end": v(-34.4, 17.5) * mm});
            skLineSegment(sketch, "E28.left", {"start": v(-31.4, 3.5) * mm, "end": v(-31.4, 17.5) * mm});
            skLineSegment(sketch, "E28.right", {"start": v(-34.4, 3.5) * mm, "end": v(-34.4, 17.5) * mm});
            skPoint(sketch, "E28.middle", {"position": v(-32.9, 10.5) * mm});
            skSolve(sketch);
        }
        {
            var Q0;
            Q0=makeQuery(id+"F47.imprint","IMPRINT",FACE,{"disambiguationData":[TD([[makeQuery(id+"F47.imprint","IMPRINT",EDGE,{"derivedFrom":sQuery(id+"F47.wireOp",EDGE,"E28.bottom")}),-1.0]])]});
            var Q1;
            Q1=makeQuery(id+"F47.imprint","IMPRINT",FACE,{"disambiguationData":[TD([[makeQuery(id+"F47.imprint","IMPRINT",EDGE,{"derivedFrom":sQuery(id+"F47.wireOp",EDGE,"E27.bottom")}),-1.0]])]});
            extrude(context, id + "F48", {"entities" : qUnion([Q0, Q1]), "operationType" : NewBodyOperationType.ADD, "depth" : .5 * mm, "offsetDistance" : 25 * mm});
        }
        {
            var Q0;
            Q0=makeQuery(id+"F48.opExtrude","CAP_EDGE",EDGE,{"disambiguationData":[OSD([sQuery(id+"F47.wireOp",EDGE,"E27.top")])],"isStart":false});
            var Q1;
            Q1=makeQuery(id+"F48.opExtrude","CAP_EDGE",EDGE,{"disambiguationData":[OSD([sQuery(id+"F47.wireOp",EDGE,"E27.bottom")])],"isStart":false});
            var Q2;
            Q2=makeQuery(id+"F48.opExtrude","CAP_EDGE",EDGE,{"disambiguationData":[OSD([sQuery(id+"F47.wireOp",EDGE,"E28.top")])],"isStart":false});
            chamfer(context, id + "F49", {"entities" : qUnion([Q0, Q1, Q2]), "chamferType" : ChamferType.TWO_OFFSETS, "width1" : 7 * mm, "oppositeDirection" : false, "width2" : .5 * mm, "tangentPropagation" : true});
        }
        {
            var Q0;
            Q0=makeQuery(id+"F48.opExtrude","CAP_EDGE",EDGE,{"disambiguationData":[OSD([sQuery(id+"F47.wireOp",EDGE,"E28.bottom")])],"isStart":false});
            chamfer(context, id + "F50", {"entities" : qUnion([Q0]), "chamferType" : ChamferType.TWO_OFFSETS, "width1" : 7 * mm, "oppositeDirection" : true, "width2" : .5 * mm, "tangentPropagation" : true});
        }
        {
            var Q0;
            Q0=makeQuery(id+"F1.opExtrude","SWEPT_FACE",FACE,{"disambiguationData":[OSD([sQuery(id+"F0.wireOp",EDGE,"E4.2")])]});
            var sketch = newSketch(context, id + "F51", { "sketchPlane" : qUnion([Q0])});
            skLineSegment(sketch, "E29.bottom", {"start": v(1.5, 3.5) * mm, "end": v(-1.5, 3.5) * mm});
            skLineSegment(sketch, "E29.top", {"start": v(1.5, 17.5) * mm, "end": v(-1.5, 17.5) * mm});
            skLineSegment(sketch, "E29.left", {"start": v(1.5, 3.5) * mm, "end": v(1.5, 17.5) * mm});
            skLineSegment(sketch, "E29.right", {"start": v(-1.5, 3.5) * mm, "end": v(-1.5, 17.5) * mm});
            skPoint(sketch, "E29.middle", {"position": v(0, 10.5) * mm});
            skSolve(sketch);
        }
        {
            var Q0;
            Q0=makeQuery(id+"F51.imprint","IMPRINT",FACE,{"disambiguationData":[TD([[makeQuery(id+"F51.imprint","IMPRINT",EDGE,{"derivedFrom":sQuery(id+"F51.wireOp",EDGE,"E29.bottom")}),-1.0]])]});
            extrude(context, id + "F52", {"entities" : qUnion([Q0]), "operationType" : NewBodyOperationType.ADD, "depth" : .5 * mm, "offsetDistance" : 25 * mm});
        }
        {
            var Q0;
            Q0=makeQuery(id+"F52.opExtrude","CAP_EDGE",EDGE,{"disambiguationData":[OSD([sQuery(id+"F51.wireOp",EDGE,"E29.top")])],"isStart":false});
            var Q1;
            Q1=makeQuery(id+"F52.opExtrude","CAP_EDGE",EDGE,{"disambiguationData":[OSD([sQuery(id+"F51.wireOp",EDGE,"E29.bottom")])],"isStart":false});
            chamfer(context, id + "F53", {"entities" : qUnion([Q0, Q1]), "chamferType" : ChamferType.TWO_OFFSETS, "width1" : 7 * mm, "oppositeDirection" : false, "width2" : .5 * mm, "tangentPropagation" : true});
        }
    });
